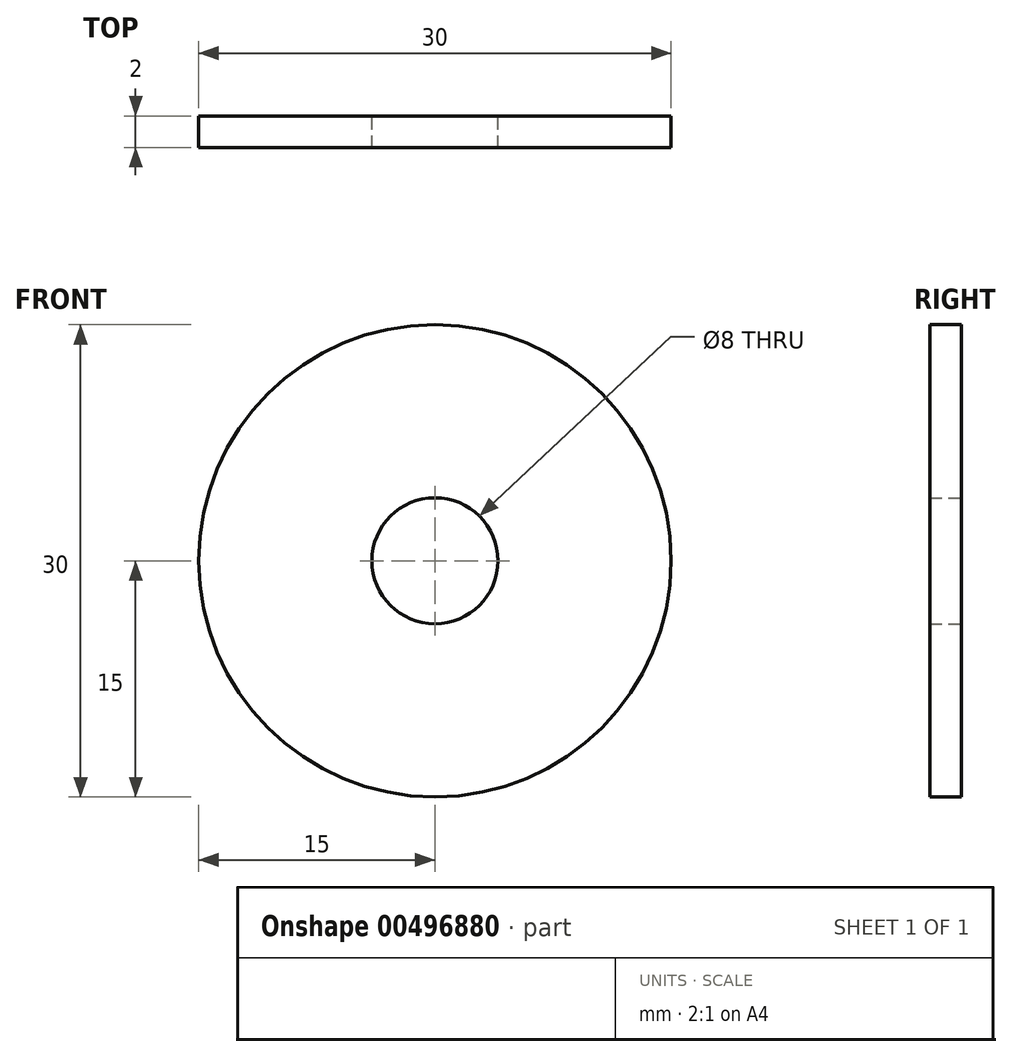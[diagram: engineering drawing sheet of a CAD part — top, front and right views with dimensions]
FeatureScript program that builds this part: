
annotation { "Feature Type Name" : "Feature", "Feature Type Description" : "" }
export const myFeature = defineFeature(function(context is Context, id is Id, definition is map)
    precondition{}
    {
        {
            var Q0;
            Q0=qCreatedBy(makeId("Front.planeOp"),FACE);
            var sketch = newSketch(context, id + "F0", { "sketchPlane" : qUnion([Q0])});
            skCircle(sketch, "E0", {"center": v(0, 0) * mm, "radius": 15 * mm});
            skCircle(sketch, "E1", {"center": v(0, 0) * mm, "radius": 4 * mm});
            skSolve(sketch);
        }
        {
            var Q0;
            Q0 = qSketchRegion(id + "F0", true);
            extrude(context, id + "F1", {"entities" : qUnion([Q0]), "depth" : 2 * mm});
        }
    });
